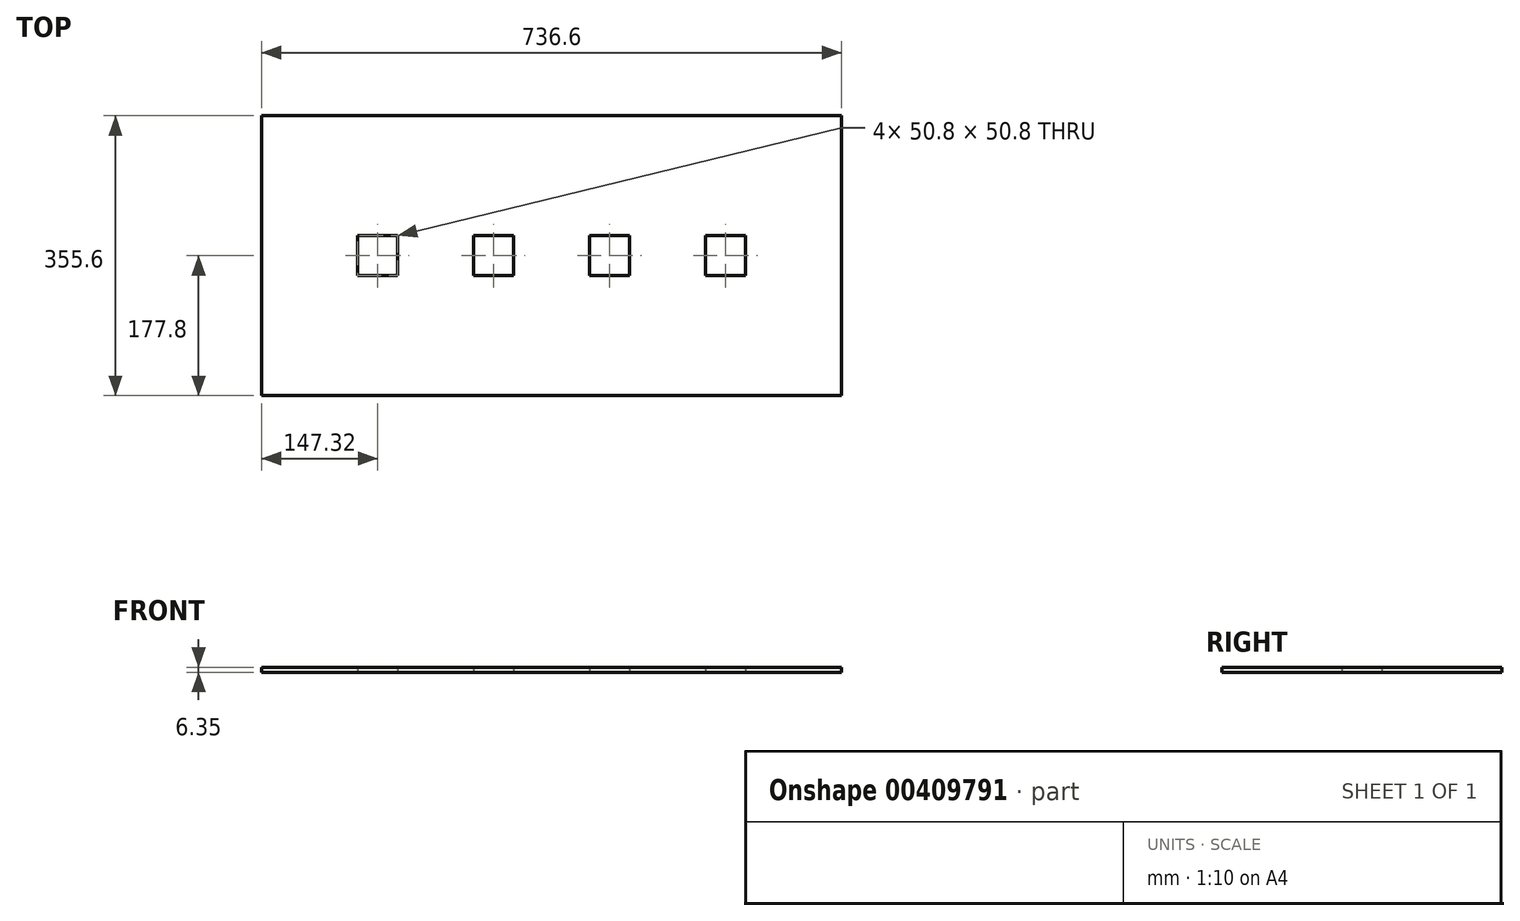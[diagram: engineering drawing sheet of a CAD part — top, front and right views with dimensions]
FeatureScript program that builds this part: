
annotation { "Feature Type Name" : "Feature", "Feature Type Description" : "" }
export const myFeature = defineFeature(function(context is Context, id is Id, definition is map)
    precondition{}
    {
        {
            var Q0;
            Q0=qCreatedBy(makeId("Top.planeOp"),FACE);
            var sketch = newSketch(context, id + "F0", { "sketchPlane" : qUnion([Q0])});
            skLineSegment(sketch, "E0.bottom", {"start": v(368.3, -177.8) * mm, "end": v(-368.3, -177.8) * mm});
            skLineSegment(sketch, "E0.top", {"start": v(368.3, 177.8) * mm, "end": v(-368.3, 177.8) * mm});
            skLineSegment(sketch, "E0.left", {"start": v(368.3, -177.8) * mm, "end": v(368.3, 177.8) * mm});
            skLineSegment(sketch, "E0.right", {"start": v(-368.3, -177.8) * mm, "end": v(-368.3, 177.8) * mm});
            skPoint(sketch, "E0.middle", {"position": v(0, 0) * mm});
            skLineSegment(sketch, "E1.bottom", {"start": v(-195.58, -25.4) * mm, "end": v(-246.38, -25.4) * mm});
            skLineSegment(sketch, "E1.top", {"start": v(-195.58, 25.4) * mm, "end": v(-246.38, 25.4) * mm});
            skLineSegment(sketch, "E1.left", {"start": v(-195.58, -25.4) * mm, "end": v(-195.58, 25.4) * mm});
            skLineSegment(sketch, "E1.right", {"start": v(-246.38, -25.4) * mm, "end": v(-246.38, 25.4) * mm});
            skPoint(sketch, "E1.middle", {"position": v(-220.98, 0) * mm});
            skLineSegment(sketch, "E2.bottom", {"start": v(-48.26, 25.4) * mm, "end": v(-99.06, 25.4) * mm});
            skLineSegment(sketch, "E2.top", {"start": v(-48.26, -25.4) * mm, "end": v(-99.06, -25.4) * mm});
            skLineSegment(sketch, "E2.left", {"start": v(-48.26, 25.4) * mm, "end": v(-48.26, -25.4) * mm});
            skLineSegment(sketch, "E2.right", {"start": v(-99.06, 25.4) * mm, "end": v(-99.06, -25.4) * mm});
            skPoint(sketch, "E2.middle", {"position": v(-73.66, 0) * mm});
            skPoint(sketch, "E2.middle.positionSnap0", {"position": v(-195.58, 0) * mm});
            skPoint(sketch, "E2.centerSnap0", {"position": v(-195.58, 0) * mm});
            skLineSegment(sketch, "E3.bottom", {"start": v(99.06, 25.4) * mm, "end": v(48.26, 25.4) * mm});
            skLineSegment(sketch, "E3.top", {"start": v(99.06, -25.4) * mm, "end": v(48.26, -25.4) * mm});
            skLineSegment(sketch, "E3.left", {"start": v(99.06, 25.4) * mm, "end": v(99.06, -25.4) * mm});
            skLineSegment(sketch, "E3.right", {"start": v(48.26, 25.4) * mm, "end": v(48.26, -25.4) * mm});
            skPoint(sketch, "E3.middle", {"position": v(73.66, 0) * mm});
            skLineSegment(sketch, "E4.bottom", {"start": v(246.38, 25.4) * mm, "end": v(195.58, 25.4) * mm});
            skLineSegment(sketch, "E4.top", {"start": v(246.38, -25.4) * mm, "end": v(195.58, -25.4) * mm});
            skLineSegment(sketch, "E4.left", {"start": v(246.38, 25.4) * mm, "end": v(246.38, -25.4) * mm});
            skLineSegment(sketch, "E4.right", {"start": v(195.58, 25.4) * mm, "end": v(195.58, -25.4) * mm});
            skPoint(sketch, "E4.middle", {"position": v(220.98, 0) * mm});
            skLineSegment(sketch, "E5", {"start": v(-220.98, 0) * mm, "end": v(-368.3, 0) * mm});
            skLineSegment(sketch, "E6", {"start": v(-220.98, 0) * mm, "end": v(-73.66, 0) * mm});
            skLineSegment(sketch, "E7", {"start": v(73.66, 0) * mm, "end": v(220.98, 0) * mm});
            skLineSegment(sketch, "E8", {"start": v(220.98, 0) * mm, "end": v(368.3, 0) * mm});
            skLineSegment(sketch, "E9", {"start": v(-73.66, 0) * mm, "end": v(73.66, 0) * mm});
            skSolve(sketch);
        }
        {
            var Q0;
            Q0=makeQuery(id+"F0.imprint","IMPRINT",FACE,{"disambiguationData":[TD([[makeQuery(id+"F0.imprint","IMPRINT",EDGE,{"derivedFrom":sQuery(id+"F0.wireOp",EDGE,"E0.bottom")}),-1.0]])]});
            var Q1;
            {var subQ8=sQuery(id+"F0.wireOp",EDGE,"E0.top");Q1=makeQuery(id+"F0.imprint","IMPRINT",FACE,{"disambiguationData":[TD([[makeQuery(id+"F0.imprint","IMPRINT",EDGE,{"derivedFrom":subQ8}),1.0]])]});}
            extrude(context, id + "F1", {"entities" : qUnion([Q0, Q1]), "depth" : 6.35 * mm});
        }
    });
